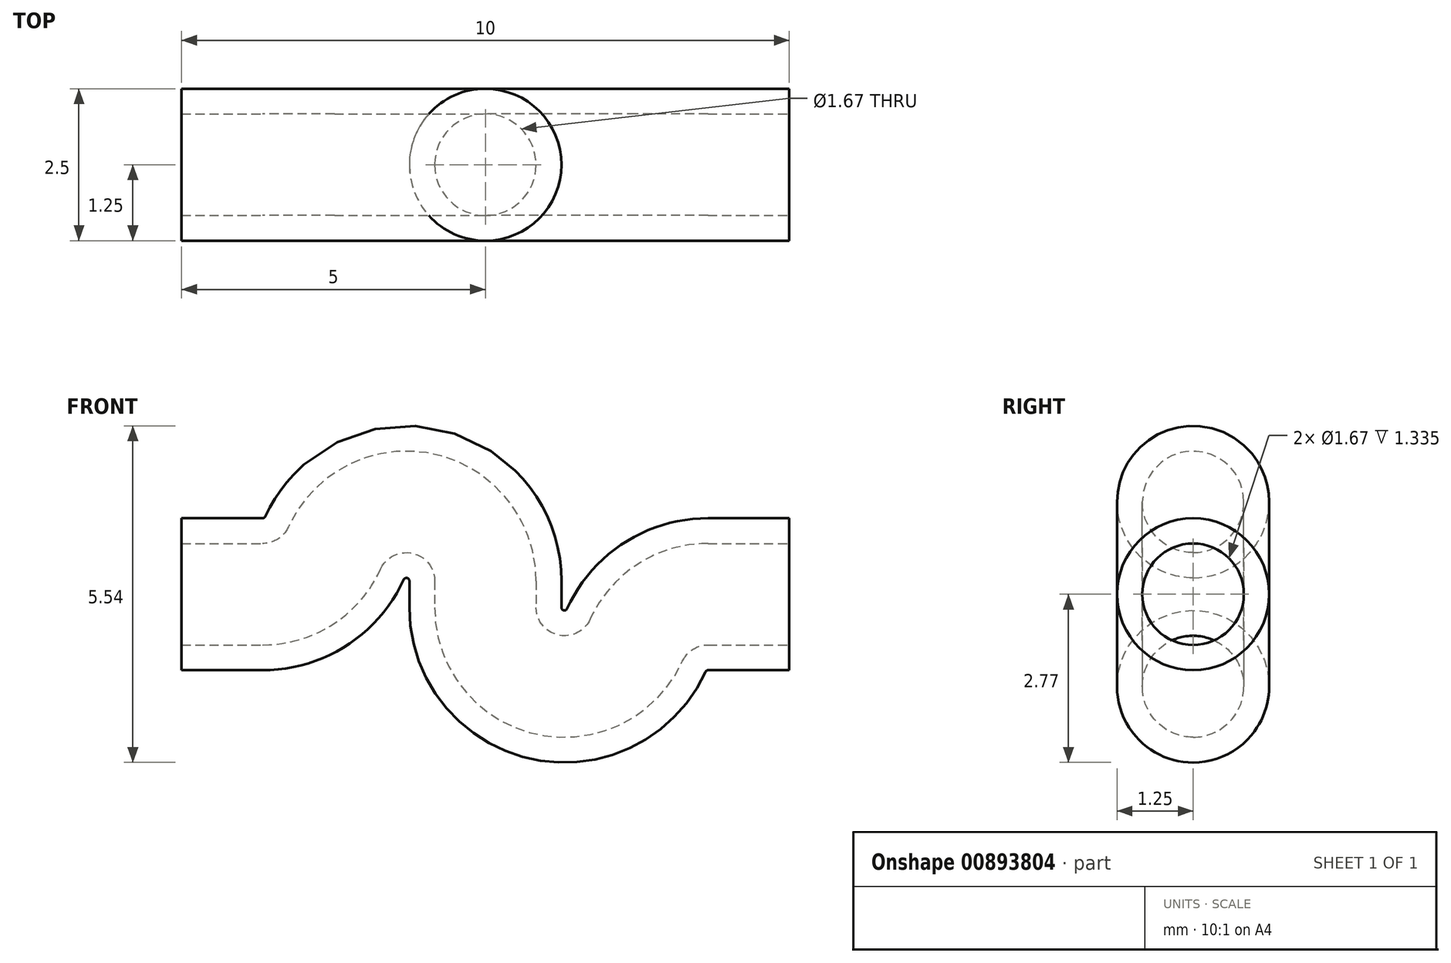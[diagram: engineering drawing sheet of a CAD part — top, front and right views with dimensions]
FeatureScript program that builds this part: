
annotation { "Feature Type Name" : "Feature", "Feature Type Description" : "" }
export const myFeature = defineFeature(function(context is Context, id is Id, definition is map)
    precondition{}
    {
        {
            var Q0;
            Q0=qCreatedBy(makeId("Front.planeOp"),FACE);
            var sketch = newSketch(context, id + "F0", { "sketchPlane" : qUnion([Q0])});
            skArc(sketch, "E0.converted", {"start": v(0, 0.22) * mm, "mid": v(-1.02, 1.5) * mm, "end": v(-2.48, 0.76) * mm});
            skLineSegment(sketch, "E1", {"start": v(0, 0.22) * mm, "end": v(0, 0) * mm});
            skArc(sketch, "E2", {"start": v(-3.67, 0) * mm, "mid": v(-2.96, 0.2) * mm, "end": v(-2.48, 0.76) * mm});
            skLineSegment(sketch, "E3", {"start": v(-2.48, 0.76) * mm, "end": v(-2.48, 0.76) * mm});
            skLineSegment(sketch, "E4.MirrorCS", {"start": v(3.67, 0) * mm, "end": v(5, 0) * mm});
            skLineSegment(sketch, "E5", {"start": v(-1.41, 0) * mm, "end": v(1.43, 0) * mm, "construction": true});
            skArc(sketch, "E6.MirrorCS", {"start": v(0, -0.22) * mm, "mid": v(1.02, -1.5) * mm, "end": v(2.48, -0.76) * mm});
            skLineSegment(sketch, "E7.MirrorCS", {"start": v(0, -0.22) * mm, "end": v(0, 0) * mm});
            skArc(sketch, "E8.MirrorCS", {"start": v(3.67, 0) * mm, "mid": v(2.96, -0.2) * mm, "end": v(2.48, -0.76) * mm});
            skLineSegment(sketch, "E9", {"start": v(-3.67, 0) * mm, "end": v(-5, 0) * mm});
            skSolve(sketch);
        }
        {
            var Q0;
            Q0=qCreatedBy(makeId("Right.planeOp"),FACE);
            var Q1;
            Q1=sQuery(id+"F0.wireOp",VERTEX,"E9.end");
            cPlane(context, id + "F1", {"entities" : qUnion([Q0, Q1]), "cplaneType" : CPlaneType.PLANE_POINT, "offset" : 25 * mm, "width" : 150 * mm, "height" : 150 * mm});
        }
        {
            var Q0;
            Q0=qCreatedBy(id+"F1.planeOp",FACE);
            var sketch = newSketch(context, id + "F2", { "sketchPlane" : qUnion([Q0])});
            skCircle(sketch, "E10", {"center": v(0, 0) * mm, "radius": 1.25 * mm});
            skCircle(sketch, "E11", {"center": v(0, 0) * mm, "radius": 0.84 * mm});
            skSolve(sketch);
        }
        {
            var Q0;
            Q0=makeQuery(id+"F2.imprint","IMPRINT",FACE,{"disambiguationData":[TD([[makeQuery(id+"F2.imprint","IMPRINT",EDGE,{"derivedFrom":sQuery(id+"F2.wireOp",EDGE,"E10")}),1.0]])]});
            var Q1;
            Q1=sQuery(id+"F0.wireOp",EDGE,"E9");
            var Q2;
            Q2=sQuery(id+"F0.wireOp",EDGE,"E2");
            var Q3;
            Q3=sQuery(id+"F0.wireOp",EDGE,"E0.converted");
            var Q4;
            Q4=sQuery(id+"F0.wireOp",EDGE,"E6.MirrorCS");
            var Q5;
            Q5=sQuery(id+"F0.wireOp",EDGE,"E8.MirrorCS");
            var Q6;
            Q6=sQuery(id+"F0.wireOp",EDGE,"E4.MirrorCS");
            var Q7;
            Q7=sQuery(id+"F0.wireOp",EDGE,"E1");
            var Q8;
            Q8=sQuery(id+"F0.wireOp",EDGE,"E7.MirrorCS");
            sweep(context, id + "F3", {"profiles" : qUnion([Q0]), "path" : qUnion([Q1, Q2, Q3, Q4, Q5, Q6, Q7, Q8])});
        }
    });
